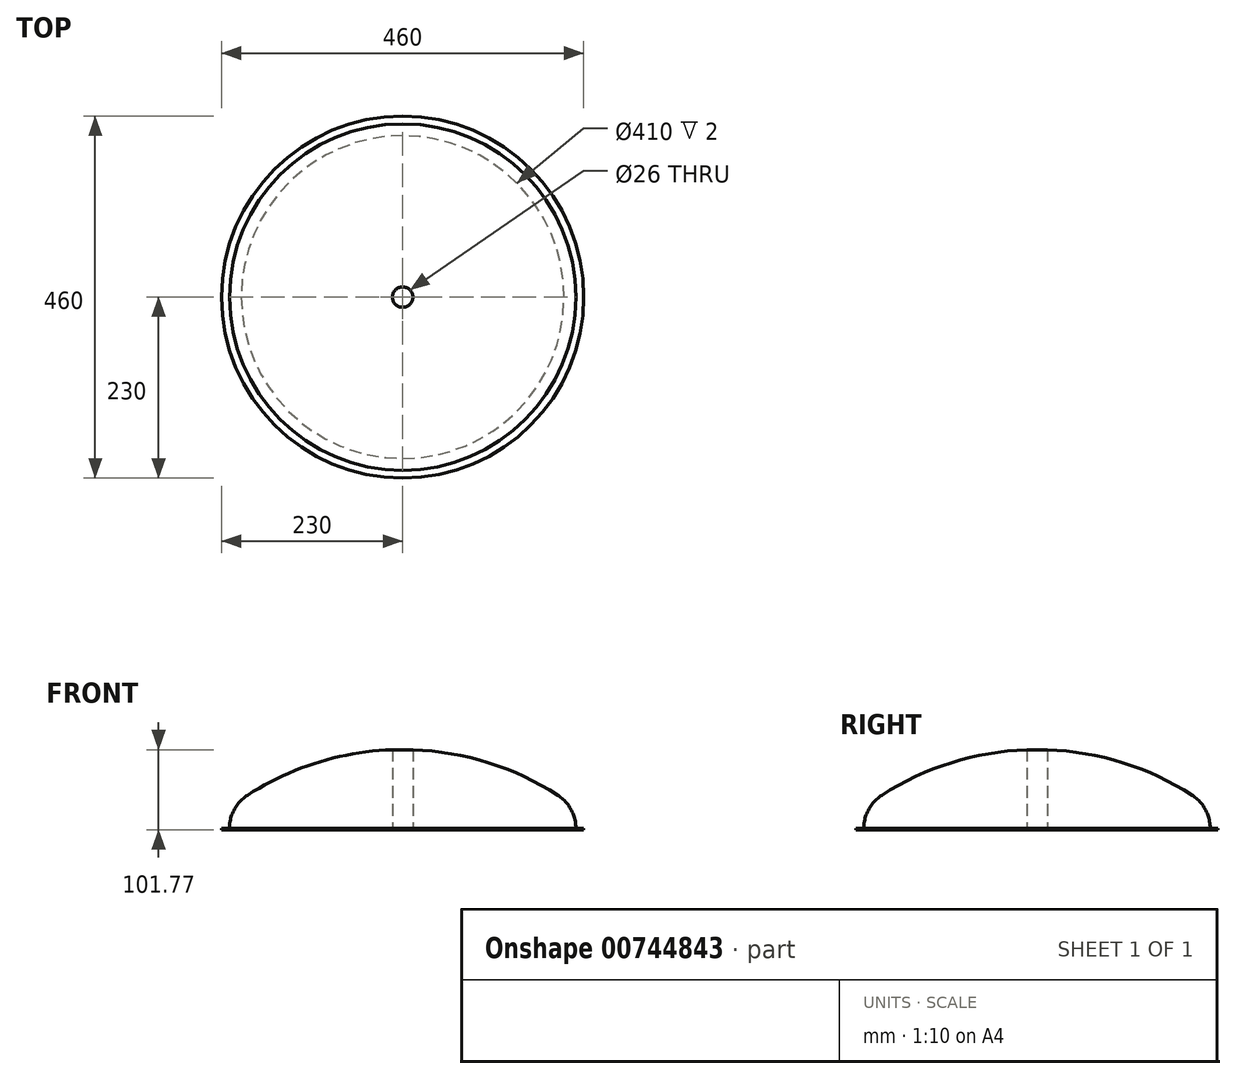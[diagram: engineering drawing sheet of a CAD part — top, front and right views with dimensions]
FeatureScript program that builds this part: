
annotation { "Feature Type Name" : "Feature", "Feature Type Description" : "" }
export const myFeature = defineFeature(function(context is Context, id is Id, definition is map)
    precondition{}
    {
        {
            var Q0;
            Q0=qCreatedBy(makeId("Front.planeOp"),FACE);
            var sketch = newSketch(context, id + "F0", { "sketchPlane" : qUnion([Q0])});
            skLineSegment(sketch, "E0", {"start": v(-220, 100) * mm, "end": v(-220, 540) * mm});
            skArc(sketch, "E1", {"start": v(0, 640) * mm, "mid": v(-102.7, 625.2) * mm, "end": v(-197.07, 582.04) * mm});
            skLineSegment(sketch, "E2", {"start": v(0, 640) * mm, "end": v(58.23, 640) * mm, "construction": true});
            skPoint(sketch, "E3.visualSharp", {"position": v(-220, 566) * mm});
            skArc(sketch, "E3.filletArc", {"start": v(-197.07, 582.04) * mm, "mid": v(-213.9, 563.94) * mm, "end": v(-220, 540) * mm});
            skArc(sketch, "E4", {"start": v(-197.07, 57.96) * mm, "mid": v(-102.7, 14.8) * mm, "end": v(0, 0) * mm});
            skPoint(sketch, "E5.visualSharp", {"position": v(-220, 74) * mm});
            skArc(sketch, "E5.filletArc", {"start": v(-220, 100) * mm, "mid": v(-213.9, 76.06) * mm, "end": v(-197.07, 57.96) * mm});
            skLineSegment(sketch, "E6", {"start": v(0, 0) * mm, "end": v(49.75, 0) * mm, "construction": true});
            skLineSegment(sketch, "E7", {"start": v(0, 640) * mm, "end": v(0, 0) * mm});
            skLineSegment(sketch, "E8", {"start": v(0, 640) * mm, "end": v(0, 722.44) * mm, "construction": true});
            skSolve(sketch);
        }
        {
            var Q0;
            Q0=makeQuery(id+"F0.imprint","IMPRINT",FACE,{"disambiguationData":[TD([[makeQuery(id+"F0.imprint","IMPRINT",EDGE,{"derivedFrom":sQuery(id+"F0.wireOp",EDGE,"E0")}),-1.0]])]});
            var Q1;
            Q1=sQuery(id+"F0.wireOp",EDGE,"E8");
            revolve(context, id + "F1", {"surfaceOperationType" : NewSurfaceOperationType.NEW, "entities" : qUnion([Q0]), "axis" : qUnion([Q1]), "revolveType" : RevolveType.FULL});
        }
        {
            var Q0;
            Q0=qCreatedBy(makeId("Top.planeOp"),FACE);
            var sketch = newSketch(context, id + "F2", { "sketchPlane" : qUnion([Q0])});
            skLineSegment(sketch, "E9", {"start": v(-160, -30) * mm, "end": v(-200, -30) * mm});
            skLineSegment(sketch, "E10", {"start": v(-200, -30) * mm, "end": v(-200, 30) * mm});
            skLineSegment(sketch, "E11", {"start": v(-200, 30) * mm, "end": v(-160, 30) * mm});
            skLineSegment(sketch, "E12", {"start": v(-200, 0) * mm, "end": v(0, 0) * mm, "construction": true});
            skLineSegment(sketch, "E13.0", {"start": v(-198, 28) * mm, "end": v(-160, 28) * mm});
            skLineSegment(sketch, "E13.1", {"start": v(-198, -28) * mm, "end": v(-198, 28) * mm});
            skLineSegment(sketch, "E13.2", {"start": v(-160, -28) * mm, "end": v(-198, -28) * mm});
            skLineSegment(sketch, "E14", {"start": v(-160, -28) * mm, "end": v(-160, -30) * mm});
            skLineSegment(sketch, "E15", {"start": v(-160, 30) * mm, "end": v(-160, 28) * mm});
            skLineSegment(sketch, "E16.1.0", {"start": v(104.25, -124.56) * mm, "end": v(123.25, -157.47) * mm});
            skLineSegment(sketch, "E16.1.1", {"start": v(123.25, -157.47) * mm, "end": v(74.75, -185.47) * mm});
            skLineSegment(sketch, "E16.1.2", {"start": v(74.75, -185.47) * mm, "end": v(55.75, -152.56) * mm});
            skLineSegment(sketch, "E16.1.3", {"start": v(125.98, -158.2) * mm, "end": v(74.02, -188.2) * mm});
            skLineSegment(sketch, "E16.1.4", {"start": v(74.02, -188.2) * mm, "end": v(54.02, -153.56) * mm});
            skLineSegment(sketch, "E16.1.5", {"start": v(105.98, -123.56) * mm, "end": v(125.98, -158.2) * mm});
            skLineSegment(sketch, "E16.1.6", {"start": v(54.02, -153.56) * mm, "end": v(55.75, -152.56) * mm});
            skLineSegment(sketch, "E16.1.7", {"start": v(104.25, -124.56) * mm, "end": v(105.98, -123.56) * mm});
            skLineSegment(sketch, "E16.2.0", {"start": v(55.75, 152.56) * mm, "end": v(74.75, 185.47) * mm});
            skLineSegment(sketch, "E16.2.1", {"start": v(74.75, 185.47) * mm, "end": v(123.25, 157.47) * mm});
            skLineSegment(sketch, "E16.2.2", {"start": v(123.25, 157.47) * mm, "end": v(104.25, 124.56) * mm});
            skLineSegment(sketch, "E16.2.3", {"start": v(74.02, 188.2) * mm, "end": v(125.98, 158.2) * mm});
            skLineSegment(sketch, "E16.2.4", {"start": v(125.98, 158.2) * mm, "end": v(105.98, 123.56) * mm});
            skLineSegment(sketch, "E16.2.5", {"start": v(54.02, 153.56) * mm, "end": v(74.02, 188.2) * mm});
            skLineSegment(sketch, "E16.2.6", {"start": v(105.98, 123.56) * mm, "end": v(104.25, 124.56) * mm});
            skLineSegment(sketch, "E16.2.7", {"start": v(55.75, 152.56) * mm, "end": v(54.02, 153.56) * mm});
            skPoint(sketch, "E16.center", {"position": v(0, 0) * mm});
            skSolve(sketch);
        }
        {
            var Q0;
            Q0=qSketchRegion(id+"F2",true);
            var Q1;
            Q1=makeQuery(id+"F1.opRevolve","SWEPT_BODY",BODY,{"disambiguationData":[OSD([sQuery(id+"F0.wireOp",EDGE,"E0"),sQuery(id+"F0.wireOp",EDGE,"E1"),sQuery(id+"F0.wireOp",EDGE,"E3.filletArc"),sQuery(id+"F0.wireOp",EDGE,"E4"),sQuery(id+"F0.wireOp",EDGE,"E5.filletArc"),sQuery(id+"F0.wireOp",EDGE,"E7")])]});
            extrude(context, id + "F3", {"entities" : qUnion([Q0]), "operationType" : NewBodyOperationType.ADD, "endBound" : BoundingType.UP_TO_BODY, "depth" : 25 * mm, "endBoundEntityBody" : qUnion([Q1]), "offsetDistance" : 25 * mm, "hasSecondDirection" : true, "secondDirectionOppositeDirection" : true, "secondDirectionDepth" : 200 * mm});
        }
        {
            var Q0;
            Q0=qCreatedBy(makeId("Front.planeOp"),FACE);
            var sketch = newSketch(context, id + "F4", { "sketchPlane" : qUnion([Q0])});
            skLineSegment(sketch, "E17.bottom", {"start": v(-283.95, 540) * mm, "end": v(306.89, 540) * mm});
            skLineSegment(sketch, "E17.top", {"start": v(-283.95, -213) * mm, "end": v(306.89, -213) * mm});
            skLineSegment(sketch, "E17.left", {"start": v(-283.95, 540) * mm, "end": v(-283.95, -213) * mm});
            skLineSegment(sketch, "E17.right", {"start": v(306.89, 540) * mm, "end": v(306.89, -213) * mm});
            skArc(sketch, "E18", {"start": v(197.07, 582.04) * mm, "mid": v(0, 640) * mm, "end": v(-197.07, 582.04) * mm});
            skPoint(sketch, "E19", {"position": v(0, 640) * mm});
            skSolve(sketch);
        }
        {
            var Q0;
            Q0 = qSketchRegion(id + "F4", true);
            extrude(context, id + "F5", {"entities" : qUnion([Q0]), "operationType" : NewBodyOperationType.REMOVE, "endBound" : BoundingType.THROUGH_ALL, "oppositeDirection" : true, "depth" : 25 * mm, "offsetDistance" : 25 * mm, "hasSecondDirection" : true, "secondDirectionBound" : SecondDirectionBoundingType.THROUGH_ALL, "secondDirectionOppositeDirection" : false, "secondDirectionDepth" : 25 * mm});
        }
        {
            var Q0;
            Q0=makeQuery(id+"F5.boolean.opBoolean","COPY",FACE,{"derivedFrom":makeQuery(id+"F5.opExtrude","SWEPT_FACE",FACE,{"disambiguationData":[OSD([sQuery(id+"F4.wireOp",EDGE,"E17.bottom")])]})});
            var sketch = newSketch(context, id + "F6", { "sketchPlane" : qUnion([Q0])});
            skCircle(sketch, "E20", {"center": v(0, 0) * mm, "radius": 230 * mm});
            skCircle(sketch, "E21", {"center": v(0, 0) * mm, "radius": 205 * mm});
            skSolve(sketch);
        }
        {
            var Q0;
            Q0 = qSketchRegion(id + "F6", true);
            extrude(context, id + "F7", {"entities" : qUnion([Q0]), "operationType" : NewBodyOperationType.ADD, "depth" : 2 * mm, "offsetDistance" : 25 * mm});
        }
        {
            var Q0;
            Q0=qCreatedBy(makeId("Top.planeOp"),FACE);
            var sketch = newSketch(context, id + "F8", { "sketchPlane" : qUnion([Q0])});
            skCircle(sketch, "E22", {"center": v(0, 0) * mm, "radius": 13 * mm});
            skSolve(sketch);
        }
        {
            var Q0;
            Q0 = qSketchRegion(id + "F8", true);
            extrude(context, id + "F9", {"entities" : qUnion([Q0]), "operationType" : NewBodyOperationType.REMOVE, "endBound" : BoundingType.THROUGH_ALL, "depth" : 25 * mm, "offsetDistance" : 25 * mm});
        }
    });
